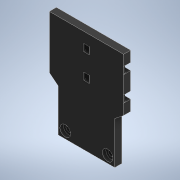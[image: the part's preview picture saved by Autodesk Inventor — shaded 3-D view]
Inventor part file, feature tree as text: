
AUTODESK INVENTOR PART (.ipt)
format: ipt  version: 2021 (Build 250183000, 183)  size: 185,344 bytes
history: native  units: mm
features: extrude x3, sketch x2, projected_geometry x2, fillet x1
ambient origin geometry x8: Origin, YZ Plane, XZ Plane, XY Plane, X Axis, Y Axis, Z Axis, Center Point
bodies: Solid1 (feature_tree)
feature tree (8):
  extrude  "Extrusion1"  Depth=42.0mm
  extrude  "Extrusion2"  Depth=4.0mm
  fillet  "Fillet1"  Radius=3.2mm
  extrude  "Extrusion3"  Depth=4.0mm TaperAngle=0.0deg
  sketch  "Sketch2"  dims[d0=30.0mm d1=42.0mm]
  sketch  "Sketch3"  dims[d2=24.0mm d3=12.0mm d5=3.2mm d6=4.0mm d7=0.0mm d8=6.0mm d10=4.0mm d11=3.0mm d12=2.0mm d13=0.0mm d14=2.0mm d15=6.0mm d16=2.0mm d17=0.0mm d18=4.0mm d19=32.0mm d20=24.0mm d21=4.0mm]
  projected_geometry  "Projected Loop1"
  projected_geometry  "Projected Loop2"
